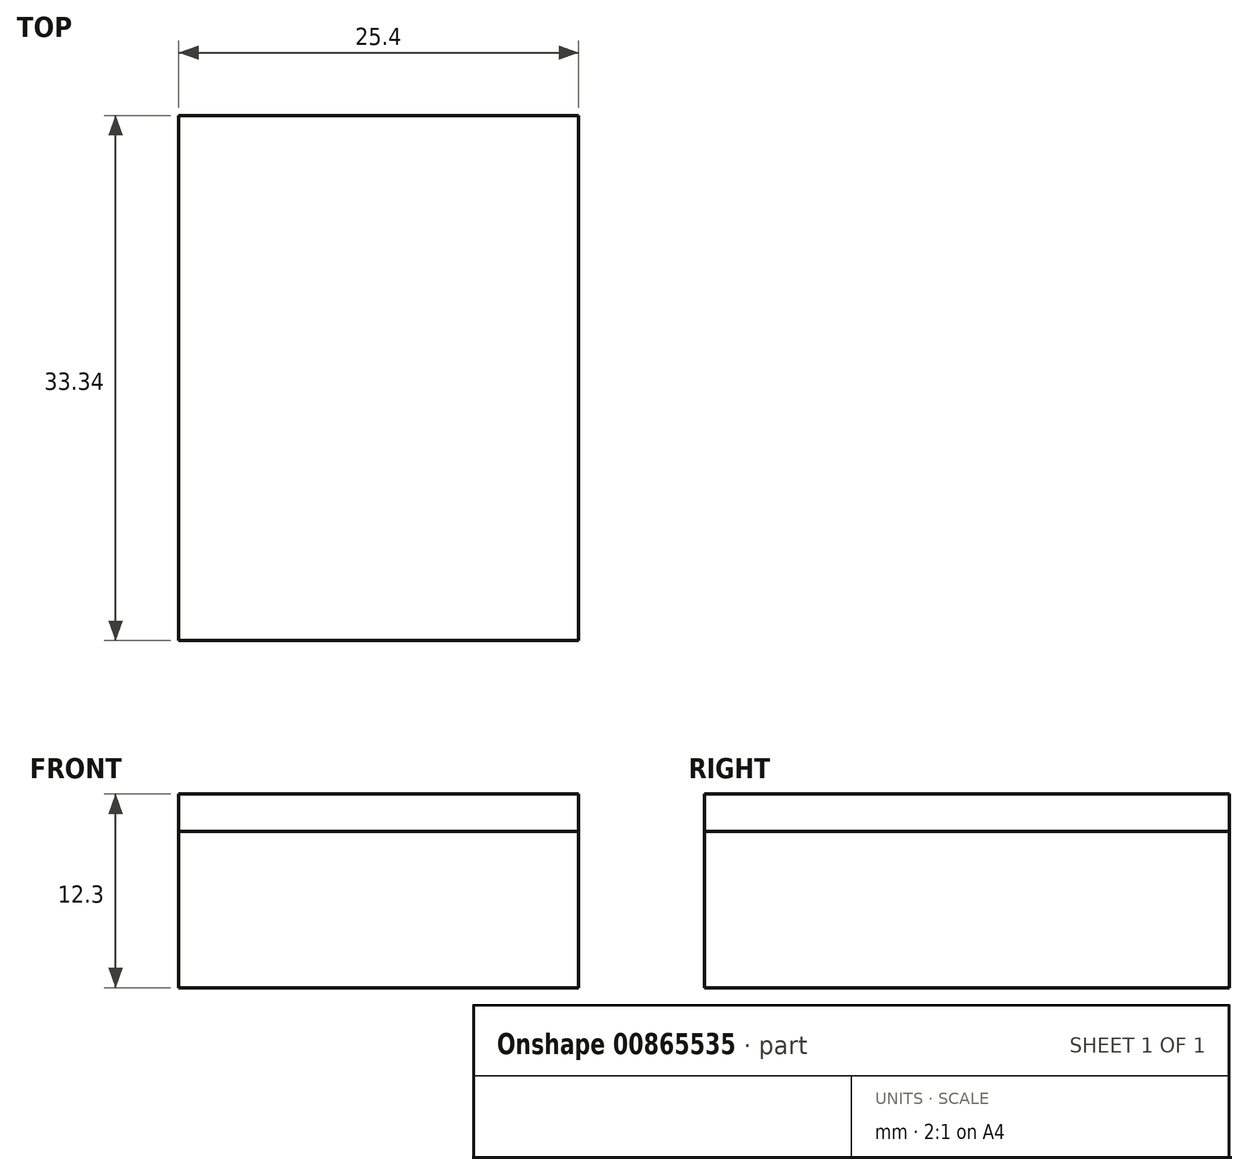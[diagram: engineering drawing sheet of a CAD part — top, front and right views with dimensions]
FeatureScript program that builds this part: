
annotation { "Feature Type Name" : "Feature", "Feature Type Description" : "" }
export const myFeature = defineFeature(function(context is Context, id is Id, definition is map)
    precondition{}
    {
        {
            var Q0;
            Q0=qCreatedBy(makeId("Front.planeOp"),FACE);
            var sketch = newSketch(context, id + "F0", { "sketchPlane" : qUnion([Q0])});
            skLineSegment(sketch, "E0.bottom", {"start": v(0, 0) * mm, "end": v(25.4, 0) * mm});
            skLineSegment(sketch, "E0.top", {"start": v(0, 9.92) * mm, "end": v(25.4, 9.92) * mm});
            skLineSegment(sketch, "E0.left", {"start": v(0, 0) * mm, "end": v(0, 9.92) * mm});
            skLineSegment(sketch, "E0.right", {"start": v(25.4, 0) * mm, "end": v(25.4, 9.92) * mm});
            skSolve(sketch);
        }
        {
            var Q0;
            Q0=makeQuery(id+"F0.imprint","IMPRINT",FACE,{"disambiguationData":[TD([[makeQuery(id+"F0.imprint","IMPRINT",EDGE,{"derivedFrom":sQuery(id+"F0.wireOp",EDGE,"E0.top")}),-1.0]])]});
            extrude(context, id + "F1", {"entities" : qUnion([Q0]), "depth" : 33.34 * mm, "offsetDistance" : 25.4 * mm});
        }
        {
            var Q0;
            Q0=qCreatedBy(makeId("Front.planeOp"),FACE);
            var sketch = newSketch(context, id + "F2", { "sketchPlane" : qUnion([Q0])});
            skLineSegment(sketch, "E1.bottom", {"start": v(0, 9.92) * mm, "end": v(25.4, 9.92) * mm});
            skLineSegment(sketch, "E1.top", {"start": v(0, 12.3) * mm, "end": v(25.4, 12.3) * mm});
            skLineSegment(sketch, "E1.left", {"start": v(0, 9.92) * mm, "end": v(0, 12.3) * mm});
            skLineSegment(sketch, "E1.right", {"start": v(25.4, 9.92) * mm, "end": v(25.4, 12.3) * mm});
            skSolve(sketch);
        }
        {
            var Q0;
            Q0=makeQuery(id+"F2.imprint","IMPRINT",FACE,{"disambiguationData":[TD([[makeQuery(id+"F2.imprint","IMPRINT",EDGE,{"derivedFrom":sQuery(id+"F2.wireOp",EDGE,"E1.bottom")}),1.0]])]});
            var Q1;
            Q1=makeQuery(id+"F2.imprint","IMPRINT",FACE,{"disambiguationData":[TD([[makeQuery(id+"F2.imprint","IMPRINT",EDGE,{"derivedFrom":sQuery(id+"F2.wireOp",EDGE,"582457e2-e852-40e0-b492-1080479f5f9a0.MirrorCS")}),-1.0]])]});
            extrude(context, id + "F3", {"entities" : qUnion([Q0, Q1]), "depth" : 33.34 * mm, "offsetDistance" : 25.4 * mm});
        }
    });
